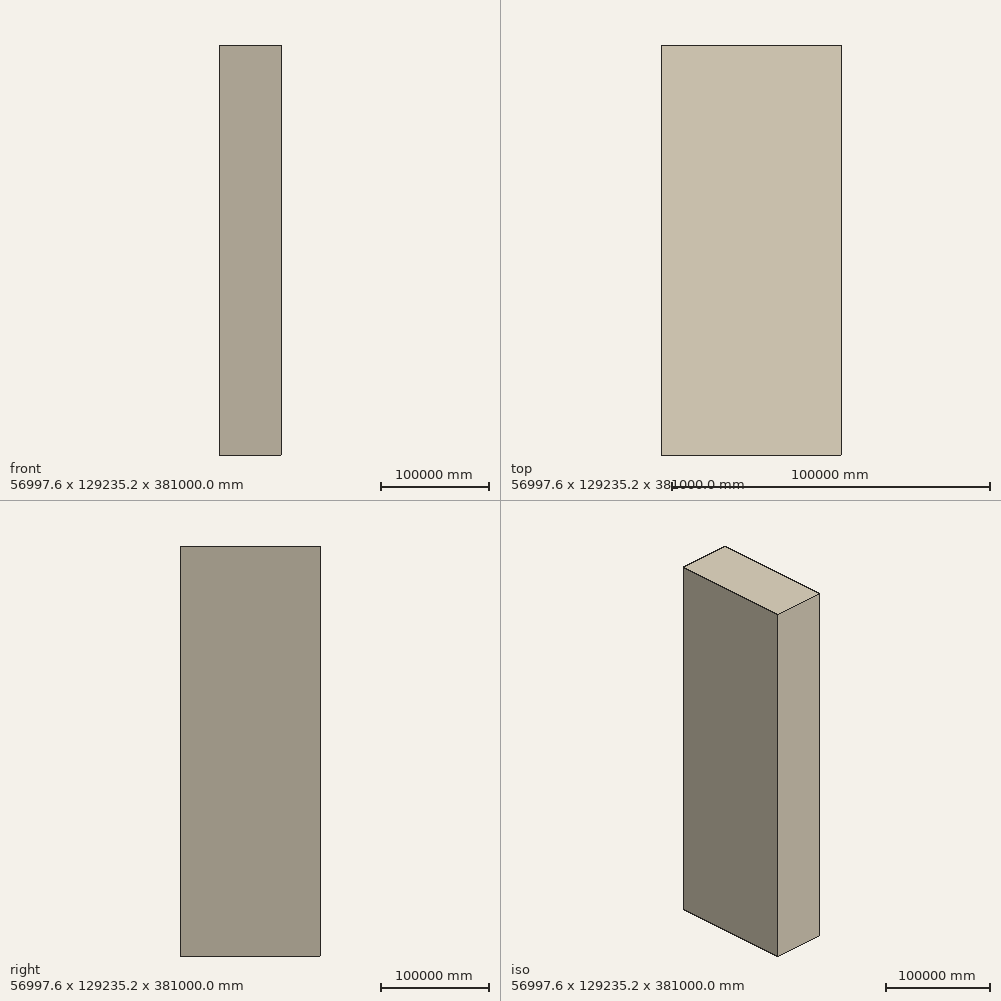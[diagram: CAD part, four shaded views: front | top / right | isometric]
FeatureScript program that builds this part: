
annotation { "Feature Type Name" : "Feature", "Feature Type Description" : "" }
export const myFeature = defineFeature(function(context is Context, id is Id, definition is map)
    precondition{}
    {
        {
            var Q0;
            Q0=qCreatedBy(makeId("Front.planeOp"),FACE);
            var sketch = newSketch(context, id + "F0", { "sketchPlane" : qUnion([Q0])});
            skLineSegment(sketch, "E0.bottom", {"start": v(0, 0) * mm, "end": v(-56997.6, 0) * mm});
            skLineSegment(sketch, "E0.top", {"start": v(0, 381000) * mm, "end": v(-56997.6, 381000) * mm});
            skLineSegment(sketch, "E0.left", {"start": v(0, 0) * mm, "end": v(0, 381000) * mm});
            skLineSegment(sketch, "E0.right", {"start": v(-56997.6, 0) * mm, "end": v(-56997.6, 381000) * mm});
            skLineSegment(sketch, "E1", {"start": v(-28498.8, 381000) * mm, "end": v(-28498.8, 443179.2) * mm});
            skSolve(sketch);
        }
        {
            var Q0;
            Q0=makeQuery(id+"F0.imprint","IMPRINT",FACE,{"disambiguationData":[TD([[makeQuery(id+"F0.imprint","IMPRINT",EDGE,{"derivedFrom":sQuery(id+"F0.wireOp",EDGE,"E0.bottom")}),-1.0]])]});
            extrude(context, id + "F1", {"entities" : qUnion([Q0]), "endBound" : BoundingType.SYMMETRIC, "depth" : 129235.2 * mm, "offsetDistance" : 30.48 * mm});
        }
        {
            var Q0;
            Q0=sQuery(id+"F0.wireOp",EDGE,"E1");
            extrude(context, id + "F2", {"bodyType" : ToolBodyType.SURFACE, "surfaceEntities" : qUnion([Q0]), "endBound" : BoundingType.SYMMETRIC, "depth" : 1524 * mm, "offsetDistance" : 30.48 * mm});
        }
    });
